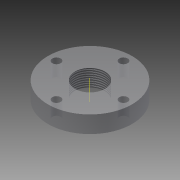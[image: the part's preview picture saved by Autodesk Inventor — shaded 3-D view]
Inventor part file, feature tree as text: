
AUTODESK INVENTOR PART (.ipt)
format: ipt  version: 2013 (Build 170138000, 138)  size: 94,208 bytes
history: native  units: in
note: dims shown in document units (in); Inventor stores cm internally (conversion verified against a paired STEP export)
features: extrude x1, thread x1, other x1, sketch x1
ambient origin geometry x8: Origin, YZ Plane, XZ Plane, XY Plane, X Axis, Y Axis, Z Axis, Center Point
bodies: Solid1 (feature_tree)
feature tree (4):
  extrude  "Extrusion1"  Depth=2.09in
  thread  "Thread1"  [1 undecoded]
  other  "Work Axis1"
  sketch  "Sketch1"  dims[d0=2.62in d1=2.09in d2=0.26in d3=0.26in d4=0.26in d5=0.26in d6=0.937in d7=0.53in d8=0.0in d9=1.0in d10=0.0in]
note: 1 required parameter value undecoded (feature->parameter linkage not recoverable at this tier; creation-order binding heuristic only, values carry confidence <= 0.55)
